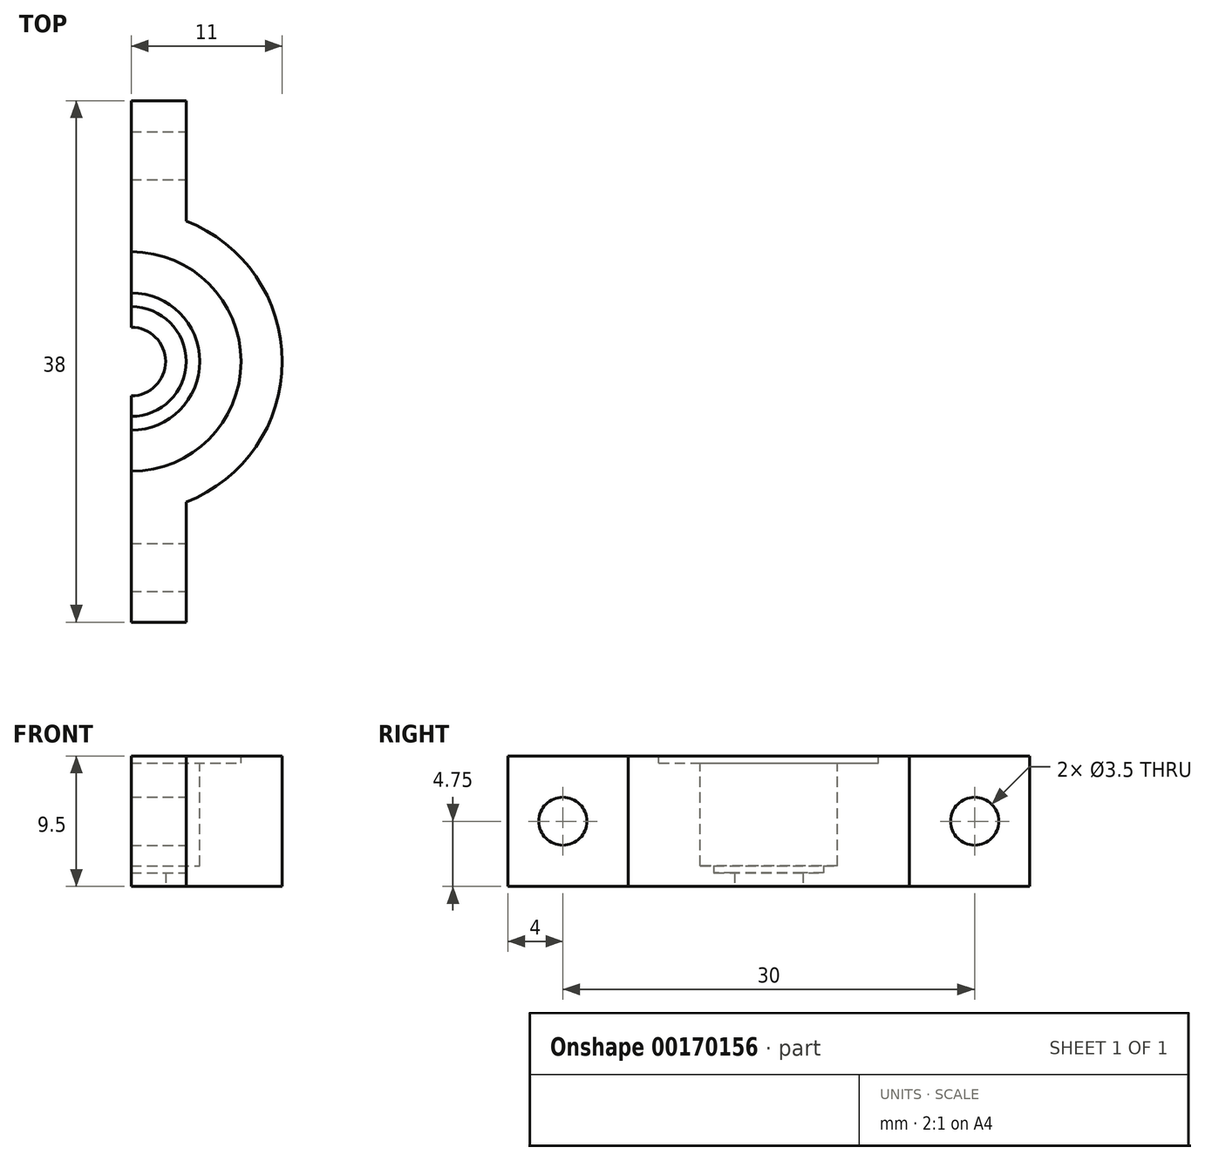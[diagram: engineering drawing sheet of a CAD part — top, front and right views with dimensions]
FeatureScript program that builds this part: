
annotation { "Feature Type Name" : "Feature", "Feature Type Description" : "" }
export const myFeature = defineFeature(function(context is Context, id is Id, definition is map)
    precondition{}
    {
        {
            var Q0;
            Q0=qCreatedBy(makeId("Top.planeOp"),FACE);
            var sketch = newSketch(context, id + "F0", { "sketchPlane" : qUnion([Q0])});
            skCircle(sketch, "E0", {"center": v(0, 0) * mm, "radius": 11 * mm});
            skSolve(sketch);
        }
        {
            var Q0;
            Q0 = qSketchRegion(id + "F0", true);
            extrude(context, id + "F1", {"entities" : qUnion([Q0]), "depth" : 9.5 * mm});
        }
        {
            var Q0;
            Q0=makeQuery(id+"F1.opExtrude","CAP_FACE",FACE,{"disambiguationData":[OSD([sQuery(id+"F0.wireOp",EDGE,"E0")])],"isStart":false});
            var sketch = newSketch(context, id + "F2", { "sketchPlane" : qUnion([Q0])});
            skCircle(sketch, "E1", {"center": v(0, 0) * mm, "radius": 8 * mm});
            skSolve(sketch);
        }
        {
            var Q0;
            Q0 = qSketchRegion(id + "F2", true);
            extrude(context, id + "F3", {"entities" : qUnion([Q0]), "operationType" : NewBodyOperationType.REMOVE, "oppositeDirection" : true, "depth" : 0.5 * mm});
        }
        {
            var Q0;
            Q0=makeQuery(id+"F3.boolean.opBoolean","COPY",FACE,{"derivedFrom":makeQuery(id+"F3.opExtrude","CAP_FACE",FACE,{"disambiguationData":[OSD([sQuery(id+"F2.wireOp",EDGE,"E1")])],"isStart":false})});
            var sketch = newSketch(context, id + "F4", { "sketchPlane" : qUnion([Q0])});
            skCircle(sketch, "E2", {"center": v(0, 0) * mm, "radius": 5 * mm});
            skSolve(sketch);
        }
        {
            var Q0;
            Q0 = qSketchRegion(id + "F4", true);
            extrude(context, id + "F5", {"entities" : qUnion([Q0]), "operationType" : NewBodyOperationType.REMOVE, "oppositeDirection" : true, "depth" : 25 * mm});
        }
        {
            var Q0;
            Q0=makeQuery(id+"F1.opExtrude","CAP_FACE",FACE,{"disambiguationData":[OSD([sQuery(id+"F0.wireOp",EDGE,"E0")])],"isStart":true});
            var sketch = newSketch(context, id + "F6", { "sketchPlane" : qUnion([Q0])});
            skCircle(sketch, "E3", {"center": v(0, 0) * mm, "radius": 2.5 * mm});
            skSolve(sketch);
        }
        {
            var Q0;
            Q0=makeQuery(id+"F6.imprint","IMPRINT",FACE,{"disambiguationData":[TD([[makeQuery(id+"F6.imprint","IMPRINT",EDGE,{"derivedFrom":sQuery(id+"F6.wireOp",EDGE,"E3")}),-1.0]])]});
            extrude(context, id + "F7", {"entities" : qUnion([Q0]), "operationType" : NewBodyOperationType.ADD, "oppositeDirection" : true, "depth" : 1 * mm});
        }
        {
            var Q0;
            Q0=makeQuery(id+"F7.opExtrude","CAP_FACE",FACE,{"disambiguationData":[OSD([sQuery(id+"F0.wireOp",EDGE,"E0"),sQuery(id+"F4.wireOp",EDGE,"E2"),sQuery(id+"F6.wireOp",EDGE,"E3")])],"isStart":false});
            var sketch = newSketch(context, id + "F8", { "sketchPlane" : qUnion([Q0])});
            skCircle(sketch, "E4", {"center": v(0, 0) * mm, "radius": 4 * mm});
            skSolve(sketch);
        }
        {
            var Q0;
            Q0=makeQuery(id+"F8.imprint","IMPRINT",FACE,{"disambiguationData":[TD([[makeQuery(id+"F8.imprint","IMPRINT",EDGE,{"derivedFrom":sQuery(id+"F8.wireOp",EDGE,"E4")}),-1.0]])]});
            extrude(context, id + "F9", {"entities" : qUnion([Q0]), "operationType" : NewBodyOperationType.ADD, "depth" : 0.5 * mm});
        }
        {
            var Q0;
            Q0=qCreatedBy(makeId("Right.planeOp"),FACE);
            var sketch = newSketch(context, id + "F10", { "sketchPlane" : qUnion([Q0])});
            skLineSegment(sketch, "E5.bottom", {"start": v(-28.05, 25.05) * mm, "end": v(34.95, 25.05) * mm});
            skLineSegment(sketch, "E5.top", {"start": v(-28.05, -17.85) * mm, "end": v(34.95, -17.85) * mm});
            skLineSegment(sketch, "E5.left", {"start": v(-28.05, 25.05) * mm, "end": v(-28.05, -17.85) * mm});
            skLineSegment(sketch, "E5.right", {"start": v(34.95, 25.05) * mm, "end": v(34.95, -17.85) * mm});
            skSolve(sketch);
        }
        {
            var Q0;
            Q0 = qSketchRegion(id + "F10", true);
            extrude(context, id + "F11", {"entities" : qUnion([Q0]), "operationType" : NewBodyOperationType.REMOVE, "oppositeDirection" : true, "depth" : 25 * mm});
        }
        {
            var Q0;
            Q0=qCreatedBy(makeId("Top.planeOp"),FACE);
            var sketch = newSketch(context, id + "F12", { "sketchPlane" : qUnion([Q0])});
            skLineSegment(sketch, "E6", {"start": v(0, -11) * mm, "end": v(0, -19) * mm});
            skLineSegment(sketch, "E7", {"start": v(0, -19) * mm, "end": v(4, -19) * mm});
            skLineSegment(sketch, "E8", {"start": v(4, -19) * mm, "end": v(4, -10.25) * mm});
            skLineSegment(sketch, "E9", {"start": v(0, 11) * mm, "end": v(0, 19) * mm});
            skLineSegment(sketch, "E10", {"start": v(0, 19) * mm, "end": v(4, 19) * mm});
            skLineSegment(sketch, "E11", {"start": v(4, 19) * mm, "end": v(4, 10.25) * mm});
            skArc(sketch, "E12", {"start": v(0, -11) * mm, "mid": v(2.04, -10.81) * mm, "end": v(4, -10.25) * mm});
            skArc(sketch, "E13.trimOffspring", {"start": v(4, 10.25) * mm, "mid": v(2.04, 10.81) * mm, "end": v(0, 11) * mm});
            skSolve(sketch);
        }
        {
            var Q0;
            Q0 = qSketchRegion(id + "F12", true);
            extrude(context, id + "F13", {"entities" : qUnion([Q0]), "operationType" : NewBodyOperationType.ADD, "depth" : 9.5 * mm});
        }
        {
            var Q0;
            Q0=makeQuery(id+"F13.opExtrude","SWEPT_FACE",FACE,{"disambiguationData":[OSD([sQuery(id+"F12.wireOp",EDGE,"E8")])]});
            var sketch = newSketch(context, id + "F14", { "sketchPlane" : qUnion([Q0])});
            skCircle(sketch, "E14", {"center": v(-15, 4.75) * mm, "radius": 1.75 * mm});
            skCircle(sketch, "E15", {"center": v(15, 4.75) * mm, "radius": 1.75 * mm});
            skSolve(sketch);
        }
        {
            var Q0;
            Q0 = qSketchRegion(id + "F14", true);
            extrude(context, id + "F15", {"entities" : qUnion([Q0]), "operationType" : NewBodyOperationType.REMOVE, "oppositeDirection" : true, "depth" : 25 * mm});
        }
    });
